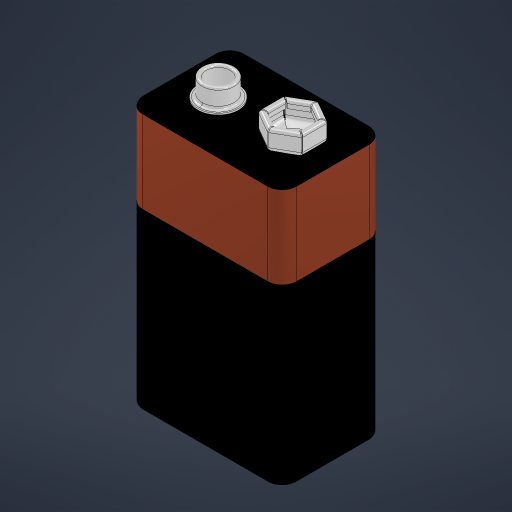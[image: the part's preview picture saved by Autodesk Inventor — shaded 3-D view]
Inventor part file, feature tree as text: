
AUTODESK INVENTOR PART (.ipt)
format: ipt  version: 2023.2 (Build 272271030, 271C)  size: 621,568 bytes
history: mixed  units: in
note: dims shown in document units (in); Inventor stores cm internally (conversion verified against a paired STEP export)
features: other x2, fillet x2, plane x1, split x1, sketch x1, mirror x1, imported_body x1
ambient origin geometry x8: Origin, YZ Plane, XZ Plane, XY Plane, X Axis, Y Axis, Z Axis, Center Point
bodies: Solid1 (imported_parasolid), Solid2 (imported_parasolid), Solid3 (imported_parasolid)
feature tree (9):
  plane  "Work Plane1"
  split  "Split1"
  other  "Decal1"
  sketch  "Sketch1"
  other  "Image2"
  mirror  "Mirror1"
  fillet  "Fillet3"  [1 undecoded]
  fillet  "Fillet10"  [1 undecoded]
  imported_body  NMx_Import_Brep_tag  [imported B-rep: ~11 faces, bbox_mm=None]
note: 2 required parameter values undecoded (feature->parameter linkage not recoverable at this tier; creation-order binding heuristic only, values carry confidence <= 0.55)
